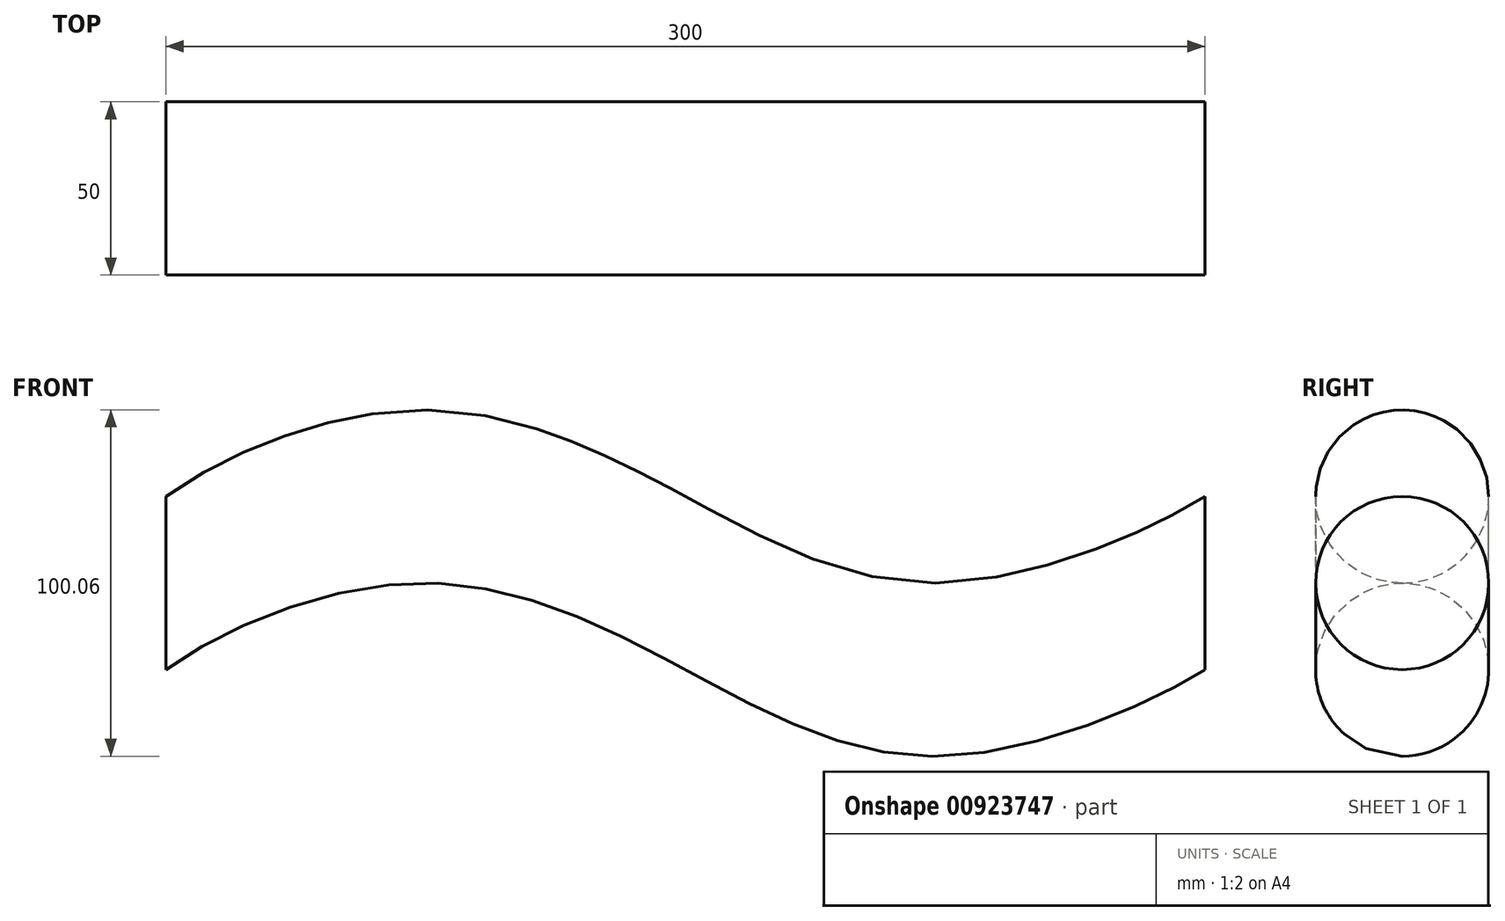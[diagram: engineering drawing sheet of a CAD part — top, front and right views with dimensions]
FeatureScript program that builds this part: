
annotation { "Feature Type Name" : "Feature", "Feature Type Description" : "" }
export const myFeature = defineFeature(function(context is Context, id is Id, definition is map)
    precondition{}
    {
        {
            var Q0;
            Q0=qCreatedBy(makeId("Right.planeOp"),FACE);
            var sketch = newSketch(context, id + "F0", { "sketchPlane" : qUnion([Q0])});
            skCircle(sketch, "E0", {"center": v(0, 0) * mm, "radius": 25 * mm});
            skSolve(sketch);
        }
        {
            var Q0;
            Q0=qCreatedBy(makeId("Front.planeOp"),FACE);
            var sketch = newSketch(context, id + "F1", { "sketchPlane" : qUnion([Q0])});
            skFitSpline(sketch, "E1", {"points": [v(0, 0) * mm, v(75, 25) * mm, v(150, 0) * mm, v(225, -25) * mm, v(300, 0) * mm], "startDerivative": vector(215.28, 156.94) * mm, "endDerivative": vector(160.31, 103.58) * mm});
            skLineSegment(sketch, "E2", {"start": v(0, 0) * mm, "end": v(300, 0) * mm, "construction": true});
            skLineSegment(sketch, "E3", {"start": v(75, 0) * mm, "end": v(75, 25) * mm, "construction": true});
            skLineSegment(sketch, "E4", {"start": v(225, 0) * mm, "end": v(225, -25) * mm, "construction": true});
            skLineSegment(sketch, "E5", {"start": v(0, 0) * mm, "end": v(0, 38.85) * mm, "construction": true});
            skSolve(sketch);
        }
        {
            var Q0;
            Q0=makeQuery(id+"F0.imprint","IMPRINT",FACE,{"disambiguationData":[TD([[makeQuery(id+"F0.imprint","IMPRINT",EDGE,{"derivedFrom":sQuery(id+"F0.wireOp",EDGE,"E0")}),1.0]])]});
            var Q1;
            Q1=sQuery(id+"F1.wireOp",EDGE,"E1");
            sweep(context, id + "F2", {"profiles" : qUnion([Q0]), "path" : qUnion([Q1]), "keepProfileOrientation" : true});
        }
    });
